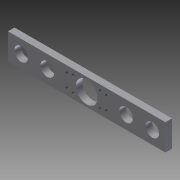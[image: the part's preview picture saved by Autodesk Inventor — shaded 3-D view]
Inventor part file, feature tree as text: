
AUTODESK INVENTOR PART (.ipt)
format: ipt  version: 2011 (Build 150239000, 239)  size: 126,464 bytes
history: native  units: in
note: dims shown in document units (in); Inventor stores cm internally (conversion verified against a paired STEP export)
features: sketch x7, hole x3, extrude x2, plane x2, mirror x2
ambient origin geometry x8: Origin, YZ Plane, XZ Plane, XY Plane, X Axis, Y Axis, Z Axis, Center Point
bodies: Solid1 (feature_tree)
feature tree (16):
  extrude  "Extrusion1"  Depth=0.374in
  extrude  "Extrusion2"  Depth=3.0in
  hole  "Hole1"  [1 undecoded]
  sketch  "Sketch5"  dims[d7=0.4134in d8=0.0625in d9=0.0in]
  plane  "Work Plane1"
  mirror  "Mirror1"
  hole  "Hole2"  [1 undecoded]
  sketch  "Sketch7"  dims[d15=120.0deg]
  plane  "Work Plane2"
  mirror  "Mirror2"
  hole  "Hole3"  [1 undecoded]
  sketch  "Sketch1"  dims[d0=0.51in d1=0.374in]
  sketch  "Sketch2"  dims[d2=0.75in d3=3.0in]
  sketch  "Sketch4"  dims[d4=0.5in d5=0.125in d6=0.0in]
  sketch  "Sketch6"  dims[d13=0.5906in d14=30.0deg]
  sketch  "Sketch8"  dims[d16=0.062in d17=0.75in d18=0.375in d19=0.25in d20=0.5635in d21=0.0315in d22=0.8108in d23=90.0deg d24=0.26in d25=0.75in d26=0.375in d27=0.25in d28=0.5635in d29=0.0315in d30=0.8108in d31=90.0deg d32=0.062in d33=0.75in d34=0.375in d35=0.25in d36=0.5635in d37=0.0315in d38=0.8108in]
note: 3 required parameter values undecoded (feature->parameter linkage not recoverable at this tier; creation-order binding heuristic only, values carry confidence <= 0.55)
